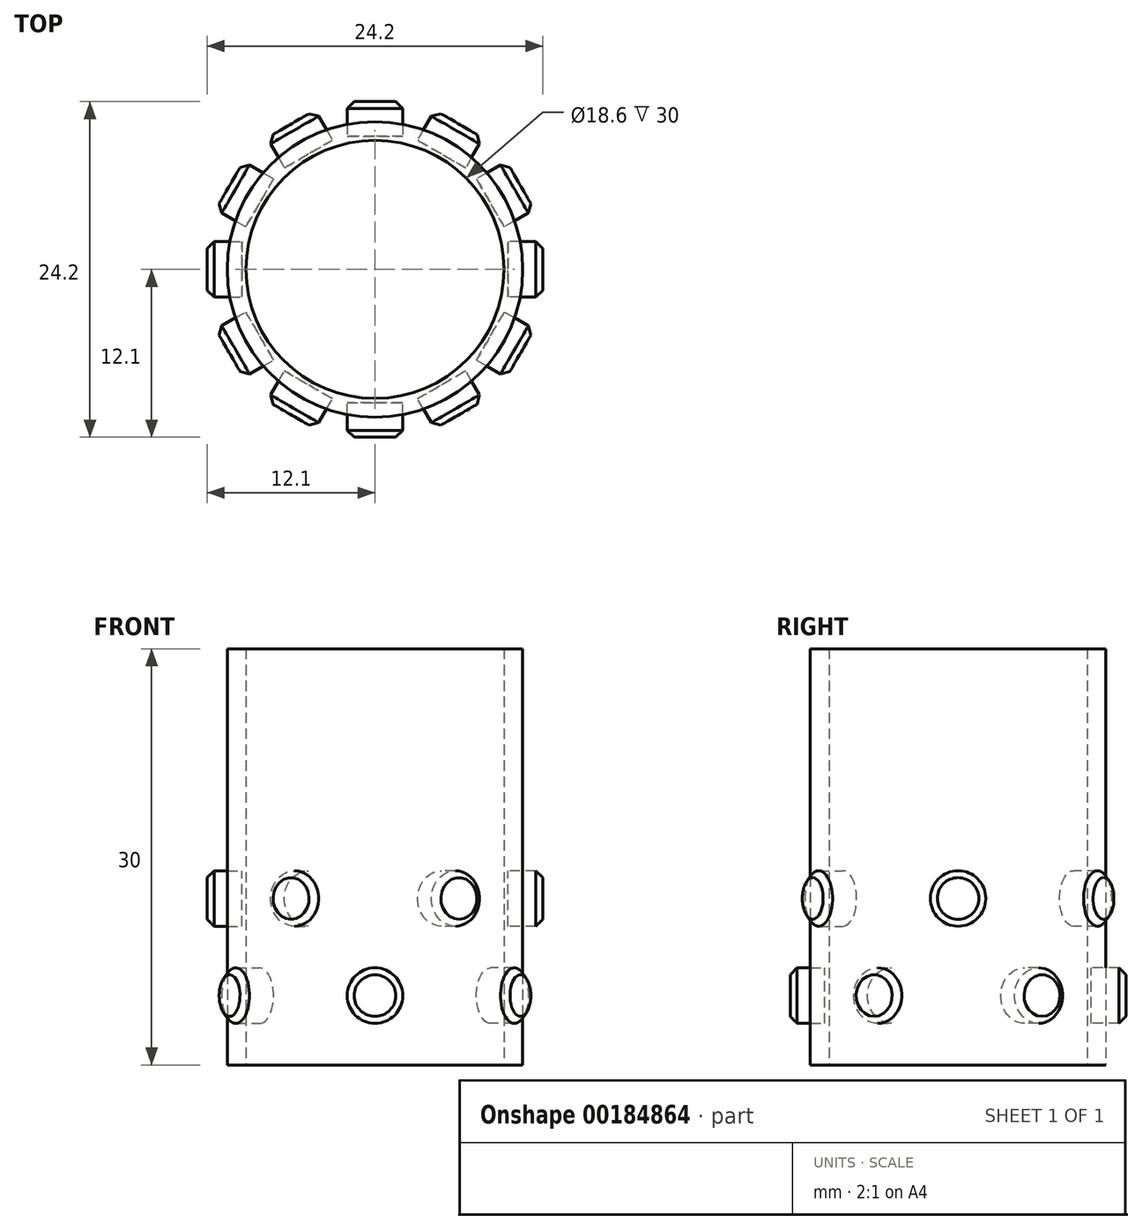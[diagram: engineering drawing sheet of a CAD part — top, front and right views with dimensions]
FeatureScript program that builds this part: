
annotation { "Feature Type Name" : "Feature", "Feature Type Description" : "" }
export const myFeature = defineFeature(function(context is Context, id is Id, definition is map)
    precondition{}
    {
        {
            var Q0;
            Q0=qCreatedBy(makeId("Top.planeOp"),FACE);
            var sketch = newSketch(context, id + "F0", { "sketchPlane" : qUnion([Q0])});
            skCircle(sketch, "E0", {"center": v(0, 0) * mm, "radius": 10.65 * mm});
            skCircle(sketch, "E1", {"center": v(0, 0) * mm, "radius": 9.3 * mm});
            skSolve(sketch);
        }
        {
            var Q0;
            Q0 = qSketchRegion(id + "F0", true);
            extrude(context, id + "F1", {"entities" : qUnion([Q0]), "depth" : 30 * mm});
        }
        {
            var Q0;
            Q0=qCreatedBy(makeId("Front.planeOp"),FACE);
            var sketch = newSketch(context, id + "F2", { "sketchPlane" : qUnion([Q0])});
            skLineSegment(sketch, "E2", {"start": v(0, 0) * mm, "end": v(0, 5) * mm});
            skCircle(sketch, "E3", {"center": v(0, 5) * mm, "radius": 2 * mm});
            skSolve(sketch);
        }
        {
            var Q0;
            Q0 = qSketchRegion(id + "F2", true);
            extrude(context, id + "F3", {"entities" : qUnion([Q0]), "depth" : 2.5 * mm});
        }
        {
            var Q0;
            Q0=makeQuery(id+"F3.opExtrude","CAP_EDGE",EDGE,{"disambiguationData":[OSD([sQuery(id+"F2.wireOp",EDGE,"E3")])],"isStart":false});
            chamfer(context, id + "F4", {"entities" : qUnion([Q0]), "width" : .5 * mm, "tangentPropagation" : true});
        }
        {
            var Q0;
            Q0=makeQuery(id+"F3.opExtrude","SWEPT_BODY",BODY,{"disambiguationData":[OSD([sQuery(id+"F2.wireOp",EDGE,"E3")])]});
            transform(context, id + "F5", {"entities" : qUnion([Q0]), "transformType" : TransformType.TRANSLATION_3D, "dx" : 0 * mm, "dy" : -9.6 * mm, "dz" : 0 * mm, "makeCopy" : false});
        }
        {
            var Q0;
            Q0=makeQuery(id+"F3.opExtrude","SWEPT_BODY",BODY,{"disambiguationData":[OSD([sQuery(id+"F2.wireOp",EDGE,"E3")])]});
            var Q1;
            Q1=makeQuery(id+"F1.opExtrude","SWEPT_FACE",FACE,{"disambiguationData":[OSD([sQuery(id+"F0.wireOp",EDGE,"E0")])]});
            var Q2;
            Q2=makeQuery(id+"F1.opExtrude","SWEPT_BODY",BODY,{"disambiguationData":[OSD([sQuery(id+"F0.wireOp",EDGE,"E0"),sQuery(id+"F0.wireOp",EDGE,"E1")])]});
            circularPattern(context, id + "F6", {"entities" : qUnion([Q0]), "axis" : qUnion([Q1]), "angle" : 360 * degree, "instanceCount" : 6, "equalSpace" : true});
        }
        {
            var Q0;
            Q0=makeQuery(id+"F3.opExtrude","SWEPT_BODY",BODY,{"disambiguationData":[OSD([sQuery(id+"F2.wireOp",EDGE,"E3")])]});
            transform(context, id + "F7", {"entities" : qUnion([Q0]), "transformType" : TransformType.TRANSLATION_3D, "dx" : 0 * mm, "dy" : 0 * mm, "dz" : 7 * mm, "makeCopy" : true});
        }
        {
            var Q0;
            Q0=makeQuery(id+"F7.opPattern","COPY",BODY,{"derivedFrom":makeQuery(id+"F3.opExtrude","SWEPT_BODY",BODY,{"disambiguationData":[OSD([sQuery(id+"F2.wireOp",EDGE,"E3")])]}),"instanceName":"1"});
            var Q1;
            Q1=makeQuery(id+"F1.opExtrude","SWEPT_FACE",FACE,{"disambiguationData":[OSD([sQuery(id+"F0.wireOp",EDGE,"E0")])]});
            transform(context, id + "F8", {"entities" : qUnion([Q0]), "transformType" : TransformType.ROTATION, "transformAxis" : qUnion([Q1]), "angle" : 30 * degree, "makeCopy" : false});
        }
        {
            var Q0;
            Q0=makeQuery(id+"F7.opPattern","COPY",BODY,{"derivedFrom":makeQuery(id+"F3.opExtrude","SWEPT_BODY",BODY,{"disambiguationData":[OSD([sQuery(id+"F2.wireOp",EDGE,"E3")])]}),"instanceName":"1"});
            var Q1;
            Q1=makeQuery(id+"F1.opExtrude","SWEPT_FACE",FACE,{"disambiguationData":[OSD([sQuery(id+"F0.wireOp",EDGE,"E0")])]});
            circularPattern(context, id + "F9", {"entities" : qUnion([Q0]), "axis" : qUnion([Q1]), "angle" : 360 * degree, "instanceCount" : 6, "equalSpace" : true});
        }
    });
